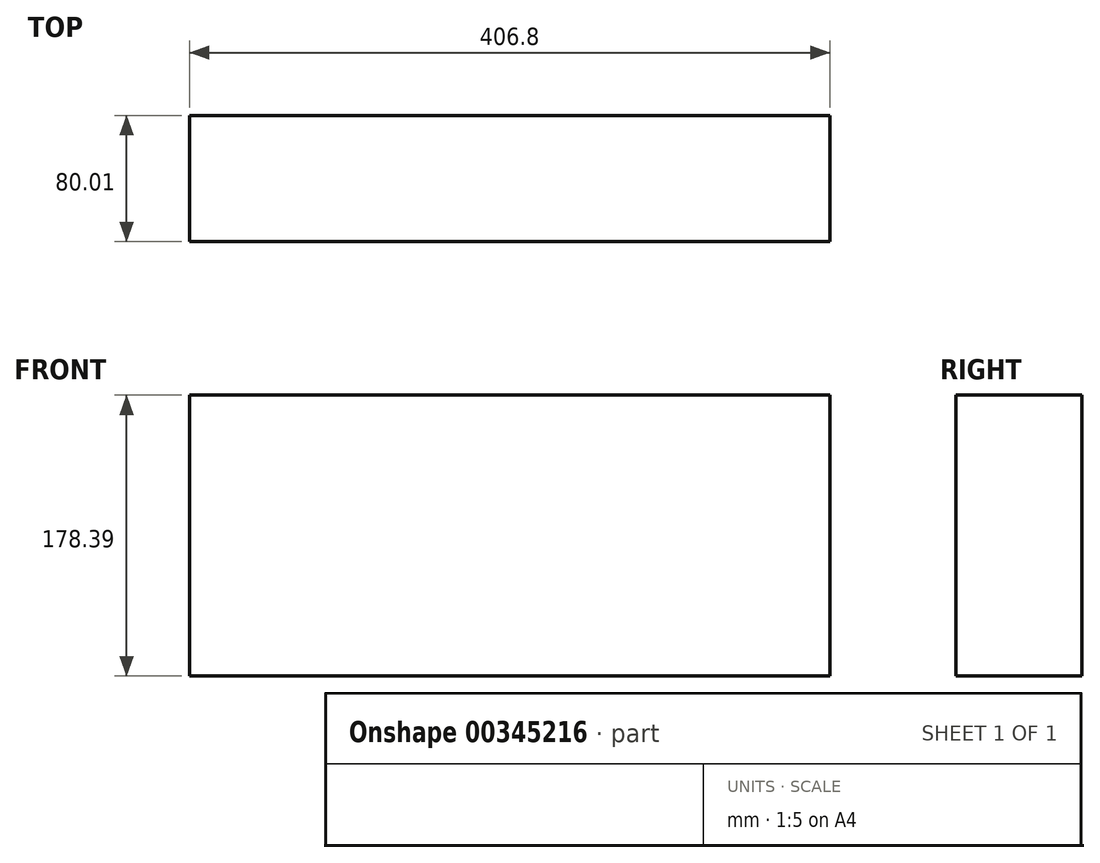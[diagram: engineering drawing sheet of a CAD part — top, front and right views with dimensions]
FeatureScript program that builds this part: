
annotation { "Feature Type Name" : "Feature", "Feature Type Description" : "" }
export const myFeature = defineFeature(function(context is Context, id is Id, definition is map)
    precondition{}
    {
        {
            var Q0;
            Q0=qCreatedBy(makeId("Front.planeOp"),FACE);
            var sketch = newSketch(context, id + "F0", { "sketchPlane" : qUnion([Q0])});
            skLineSegment(sketch, "E0.bottom", {"start": v(-47.83, 157.64) * mm, "end": v(358.97, 157.64) * mm});
            skLineSegment(sketch, "E0.top", {"start": v(-47.83, -20.75) * mm, "end": v(358.97, -20.75) * mm});
            skLineSegment(sketch, "E0.left", {"start": v(-47.83, 157.64) * mm, "end": v(-47.83, -20.75) * mm});
            skLineSegment(sketch, "E0.right", {"start": v(358.97, 157.64) * mm, "end": v(358.97, -20.75) * mm});
            skSolve(sketch);
        }
        {
            var Q0;
            Q0=makeQuery(id+"F0.imprint","IMPRINT",FACE,{"disambiguationData":[TD([[makeQuery(id+"F0.imprint","IMPRINT",EDGE,{"derivedFrom":sQuery(id+"F0.wireOp",EDGE,"E0.bottom")}),-1.0]])]});
            extrude(context, id + "F1", {"entities" : qUnion([Q0]), "oppositeDirection" : true, "depth" : 80 * mm});
        }
    });
